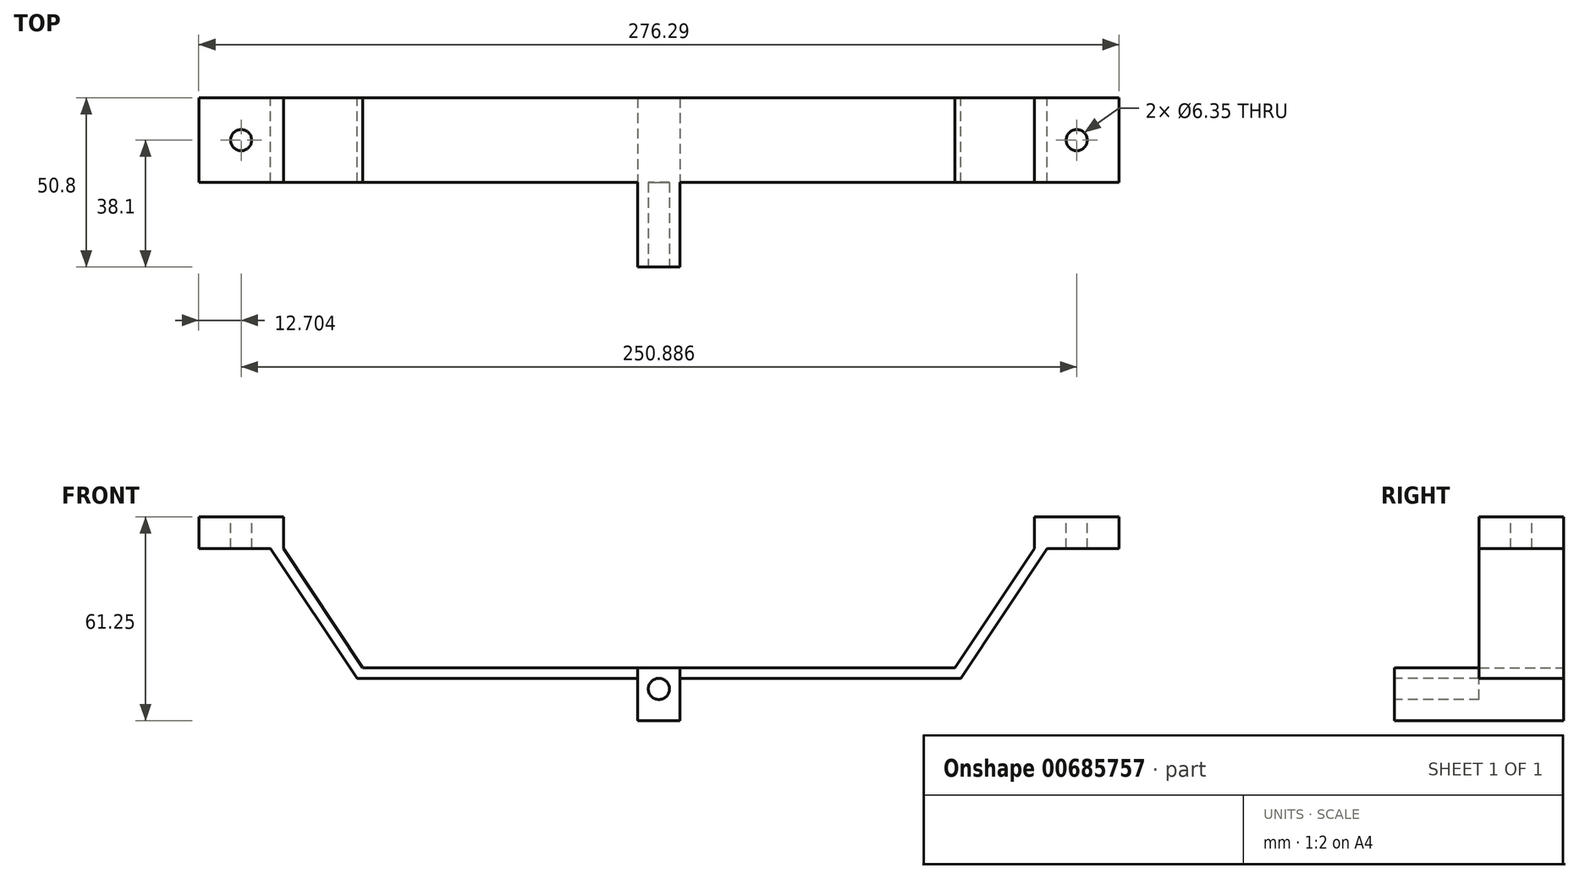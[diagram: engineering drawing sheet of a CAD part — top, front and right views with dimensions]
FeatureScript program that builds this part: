
annotation { "Feature Type Name" : "Feature", "Feature Type Description" : "" }
export const myFeature = defineFeature(function(context is Context, id is Id, definition is map)
    precondition{}
    {
        {
            var Q0;
            Q0=qCreatedBy(makeId("Front.planeOp"),FACE);
            var sketch = newSketch(context, id + "F0", { "sketchPlane" : qUnion([Q0])});
            skLineSegment(sketch, "E0", {"start": v(-83.3, 0) * mm, "end": v(94.5, 0) * mm});
            skLineSegment(sketch, "E1", {"start": v(94.5, 0) * mm, "end": v(118.35, 35.85) * mm});
            skLineSegment(sketch, "E2", {"start": v(-83.3, 0) * mm, "end": v(-107.14, 35.85) * mm});
            skLineSegment(sketch, "E3.bottom", {"start": v(-107.14, 35.85) * mm, "end": v(-132.54, 35.85) * mm});
            skLineSegment(sketch, "E3.top", {"start": v(-107.14, 45.37) * mm, "end": v(-132.54, 45.37) * mm});
            skLineSegment(sketch, "E3.left", {"start": v(-107.14, 35.85) * mm, "end": v(-107.14, 45.37) * mm});
            skLineSegment(sketch, "E3.right", {"start": v(-132.54, 35.85) * mm, "end": v(-132.54, 45.37) * mm});
            skPoint(sketch, "E4.oppositeSnap0", {"position": v(-119.84, 45.37) * mm});
            skLineSegment(sketch, "E4.bottom", {"start": v(118.35, 35.85) * mm, "end": v(143.75, 35.85) * mm});
            skLineSegment(sketch, "E4.top", {"start": v(118.35, 45.37) * mm, "end": v(143.75, 45.37) * mm});
            skLineSegment(sketch, "E4.left", {"start": v(118.35, 35.85) * mm, "end": v(118.35, 45.37) * mm});
            skLineSegment(sketch, "E4.right", {"start": v(143.75, 35.85) * mm, "end": v(143.75, 45.37) * mm});
            skLineSegment(sketch, "E5.0", {"start": v(-85, -3.18) * mm, "end": v(-109.78, 34.1) * mm});
            skLineSegment(sketch, "E5.1", {"start": v(-85, -3.17) * mm, "end": v(96.2, -3.17) * mm});
            skLineSegment(sketch, "E5.2", {"start": v(96.2, -3.18) * mm, "end": v(130.94, 49.04) * mm});
            skLineSegment(sketch, "E6", {"start": v(-109.78, 34.1) * mm, "end": v(-114.55, 41.26) * mm});
            skSolve(sketch);
        }
        {
            var Q0;
            {var subQ0=sQuery(id+"F0.wireOp",EDGE,"xCdVj7Rm-zJCy-WNEK-jx2k-DkXjC7Dfvp6H");Q0=makeQuery(id+"F0.imprint","IMPRINT",FACE,{"disambiguationData":[TD([[makeQuery(id+"F0.imprint","IMPRINT",EDGE,{"derivedFrom":subQ0}),1.0]])]});}
            var Q1;
            {var subQ0=sQuery(id+"F0.wireOp",EDGE,"zULIQO5D-5NXs-XkT0-v7lp-MGDDdhXP3ip7.right");Q1=makeQuery(id+"F0.imprint","IMPRINT",FACE,{"disambiguationData":[TD([[makeQuery(id+"F0.imprint","IMPRINT",EDGE,{"derivedFrom":subQ0}),-1.0]])]});}
            var Q2;
            {var subQ0=sQuery(id+"F0.wireOp",EDGE,"zULIQO5D-5NXs-XkT0-v7lp-MGDDdhXP3ip7.left");Q2=makeQuery(id+"F0.imprint","IMPRINT",FACE,{"disambiguationData":[TD([[makeQuery(id+"F0.imprint","IMPRINT",EDGE,{"derivedFrom":subQ0}),1.0]])]});}
            var Q3;
            {var subQ4=sQuery(id+"F0.wireOp",EDGE,"WJLMLYwR-hRPP-A6Xb-pmzy-IOSkZiBtCFEh.left");Q3=makeQuery(id+"F0.imprint","IMPRINT",FACE,{"disambiguationData":[TD([[makeQuery(id+"F0.imprint","IMPRINT",EDGE,{"derivedFrom":subQ4}),1.0]])]});}
            var Q4;
            {var subQ4=sQuery(id+"F0.wireOp",EDGE,"WJLMLYwR-hRPP-A6Xb-pmzy-IOSkZiBtCFEh.right");Q4=makeQuery(id+"F0.imprint","IMPRINT",FACE,{"disambiguationData":[TD([[makeQuery(id+"F0.imprint","IMPRINT",EDGE,{"derivedFrom":subQ4}),-1.0]])]});}
            var Q5;
            {var subQ0=sQuery(id+"F0.wireOp",EDGE,"45bcc17d-5c14-4652-9b34-e62cf62e381f0.MirrorCS");Q5=makeQuery(id+"F0.imprint","IMPRINT",FACE,{"disambiguationData":[TD([[makeQuery(id+"F0.imprint","IMPRINT",EDGE,{"derivedFrom":subQ0}),1.0]])]});}
            var Q6;
            {var subQ0=sQuery(id+"F0.wireOp",EDGE,"87b93818-efcd-4817-b442-400501f782e70.MirrorCS");Q6=makeQuery(id+"F0.imprint","IMPRINT",FACE,{"disambiguationData":[TD([[makeQuery(id+"F0.imprint","IMPRINT",EDGE,{"derivedFrom":subQ0}),-1.0]])]});}
            var Q7;
            {var subQ1=sQuery(id+"F0.wireOp",EDGE,"772e4d75-e6f5-403f-9652-c3a24cc509a90.MirrorCS");Q7=makeQuery(id+"F0.imprint","IMPRINT",FACE,{"disambiguationData":[TD([[makeQuery(id+"F0.imprint","IMPRINT",EDGE,{"derivedFrom":subQ1}),1.0]])]});}
            var Q8;
            {var subQ4=sQuery(id+"F0.wireOp",EDGE,"8517a0ab-6009-46a5-8872-56797a2ff2e90.MirrorCS");Q8=makeQuery(id+"F0.imprint","IMPRINT",FACE,{"disambiguationData":[TD([[makeQuery(id+"F0.imprint","IMPRINT",EDGE,{"derivedFrom":subQ4}),1.0]])]});}
            var Q9;
            {var subQ1=sQuery(id+"F0.wireOp",EDGE,"7d77567f-4d39-41c3-929c-f897b328c47e0.MirrorCS");Q9=makeQuery(id+"F0.imprint","IMPRINT",FACE,{"disambiguationData":[TD([[makeQuery(id+"F0.imprint","IMPRINT",EDGE,{"derivedFrom":subQ1}),-1.0]])]});}
            var Q10;
            Q10=makeQuery(id+"F0.imprint","IMPRINT",FACE,{"disambiguationData":[TD([[makeQuery(id+"F0.imprint","IMPRINT",EDGE,{"derivedFrom":sQuery(id+"F0.wireOp",EDGE,"E3.top")}),1.0]])]});
            var Q11;
            Q11=makeQuery(id+"F0.imprint","IMPRINT",FACE,{"disambiguationData":[TD([[makeQuery(id+"F0.imprint","IMPRINT",EDGE,{"derivedFrom":sQuery(id+"F0.wireOp",EDGE,"E0")}),-1.0]])]});
            var Q12;
            {var subQ0=sQuery(id+"F0.wireOp",EDGE,"E4.left");Q12=makeQuery(id+"F0.imprint","IMPRINT",FACE,{"disambiguationData":[TD([[makeQuery(id+"F0.imprint","IMPRINT",EDGE,{"derivedFrom":subQ0}),-1.0]])]});}
            var Q13;
            {var subQ0=sQuery(id+"F0.wireOp",EDGE,"E4.right");Q13=makeQuery(id+"F0.imprint","IMPRINT",FACE,{"disambiguationData":[TD([[makeQuery(id+"F0.imprint","IMPRINT",EDGE,{"derivedFrom":subQ0}),1.0]])]});}
            extrude(context, id + "F1", {"entities" : qUnion([Q0, Q1, Q2, Q3, Q4, Q5, Q6, Q7, Q8, Q9, Q10, Q11, Q12, Q13]), "endBound" : BoundingType.SYMMETRIC, "depth" : 25.4 * mm});
        }
        {
            var Q0;
            Q0=makeQuery(id+"F1.opExtrude","CAP_FACE",FACE,{"disambiguationData":[OSD([sQuery(id+"F0.wireOp",EDGE,"E0"),sQuery(id+"F0.wireOp",EDGE,"E1"),sQuery(id+"F0.wireOp",EDGE,"E2"),sQuery(id+"F0.wireOp",EDGE,"E3.bottom"),sQuery(id+"F0.wireOp",EDGE,"E3.top"),sQuery(id+"F0.wireOp",EDGE,"E3.left"),sQuery(id+"F0.wireOp",EDGE,"E3.right"),sQuery(id+"F0.wireOp",EDGE,"E4.bottom"),sQuery(id+"F0.wireOp",EDGE,"E4.top"),sQuery(id+"F0.wireOp",EDGE,"E4.left"),sQuery(id+"F0.wireOp",EDGE,"E4.right"),sQuery(id+"F0.wireOp",EDGE,"E5.0"),sQuery(id+"F0.wireOp",EDGE,"E5.1"),sQuery(id+"F0.wireOp",EDGE,"E5.2"),sQuery(id+"F0.wireOp",EDGE,"E6")])],"isStart":false});
            var sketch = newSketch(context, id + "F2", { "sketchPlane" : qUnion([Q0])});
            skLineSegment(sketch, "E7", {"start": v(5.6, 0) * mm, "end": v(5.6, -15.88) * mm});
            skLineSegment(sketch, "E8", {"start": v(5.6, -15.88) * mm, "end": v(11.96, -15.88) * mm});
            skLineSegment(sketch, "E9", {"start": v(5.6, -15.88) * mm, "end": v(-0.74, -15.88) * mm});
            skLineSegment(sketch, "E10", {"start": v(-0.74, -15.88) * mm, "end": v(-0.74, -3.17) * mm});
            skLineSegment(sketch, "E11", {"start": v(11.96, -15.88) * mm, "end": v(11.96, -3.17) * mm});
            skLineSegment(sketch, "E12", {"start": v(-0.74, -3.17) * mm, "end": v(-0.74, 0) * mm});
            skLineSegment(sketch, "E13", {"start": v(11.96, -3.17) * mm, "end": v(11.96, 0) * mm});
            skLineSegment(sketch, "E14", {"start": v(11.96, 0) * mm, "end": v(0, 0) * mm});
            skLineSegment(sketch, "E15", {"start": v(0, 0) * mm, "end": v(-0.74, 0) * mm});
            skSolve(sketch);
        }
        {
            var Q0;
            {var subQ0=sQuery(id+"F2.wireOp",EDGE,"E9");Q0=makeQuery(id+"F2.imprint","IMPRINT",FACE,{"disambiguationData":[TD([[makeQuery(id+"F2.imprint","IMPRINT",EDGE,{"derivedFrom":subQ0}),-1.0]])]});}
            var Q1;
            {var subQ0=sQuery(id+"F2.wireOp",EDGE,"E8");Q1=makeQuery(id+"F2.imprint","IMPRINT",FACE,{"disambiguationData":[TD([[makeQuery(id+"F2.imprint","IMPRINT",EDGE,{"derivedFrom":subQ0}),1.0]])]});}
            var Q2;
            {var subQ5=sQuery(id+"F2.wireOp",EDGE,"E13");Q2=makeQuery(id+"F2.imprint","IMPRINT",FACE,{"disambiguationData":[TD([[makeQuery(id+"F2.imprint","IMPRINT",EDGE,{"derivedFrom":subQ5}),1.0]])]});}
            var Q3;
            {var subQ4=sQuery(id+"F2.wireOp",EDGE,"E12");Q3=makeQuery(id+"F2.imprint","IMPRINT",FACE,{"disambiguationData":[TD([[makeQuery(id+"F2.imprint","IMPRINT",EDGE,{"derivedFrom":subQ4}),-1.0]])]});}
            extrude(context, id + "F3", {"entities" : qUnion([Q0, Q1, Q2, Q3]), "operationType" : NewBodyOperationType.ADD, "endBound" : BoundingType.SYMMETRIC, "depth" : 50.8 * mm});
        }
        {
            var Q0;
            Q0=makeQuery(id+"F3.opExtrude","CAP_FACE",FACE,{"disambiguationData":[OSD([sQuery(id+"F2.wireOp",EDGE,"E8"),sQuery(id+"F2.wireOp",EDGE,"E9"),sQuery(id+"F2.wireOp",EDGE,"E10"),sQuery(id+"F2.wireOp",EDGE,"E11"),sQuery(id+"F2.wireOp",EDGE,"E12"),sQuery(id+"F2.wireOp",EDGE,"E13"),sQuery(id+"F2.wireOp",EDGE,"E14"),sQuery(id+"F2.wireOp",EDGE,"E15")])],"isStart":false});
            var sketch = newSketch(context, id + "F4", { "sketchPlane" : qUnion([Q0])});
            skPoint(sketch, "E16", {"position": v(5.6, -6.35) * mm});
            skCircle(sketch, "E17", {"center": v(5.6, -6.35) * mm, "radius": 3.18 * mm});
            skSolve(sketch);
        }
        {
            var Q0;
            Q0=makeQuery(id+"F4.imprint","IMPRINT",FACE,{"disambiguationData":[TD([[makeQuery(id+"F4.imprint","IMPRINT",EDGE,{"derivedFrom":sQuery(id+"F4.wireOp",EDGE,"E17")}),1.0]])]});
            extrude(context, id + "F5", {"entities" : qUnion([Q0]), "oppositeDirection" : true, "depth" : 25.4 * mm});
        }
        {
            var Q0;
            Q0=makeQuery(id+"F1.opExtrude","SWEPT_FACE",FACE,{"disambiguationData":[OSD([sQuery(id+"F0.wireOp",EDGE,"E4.top")])]});
            var sketch = newSketch(context, id + "F6", { "sketchPlane" : qUnion([Q0])});
            skPoint(sketch, "E18", {"position": v(131.05, 0) * mm});
            skCircle(sketch, "E19", {"center": v(131.05, 0) * mm, "radius": 3.18 * mm});
            skSolve(sketch);
        }
        {
            var Q0;
            Q0=makeQuery(id+"F6.imprint","IMPRINT",FACE,{"disambiguationData":[TD([[makeQuery(id+"F6.imprint","IMPRINT",EDGE,{"derivedFrom":sQuery(id+"F6.wireOp",EDGE,"E19")}),1.0]])]});
            extrude(context, id + "F7", {"entities" : qUnion([Q0]), "operationType" : NewBodyOperationType.REMOVE, "oppositeDirection" : true, "depth" : 25.4 * mm});
        }
        {
            var Q0;
            Q0=makeQuery(id+"F1.opExtrude","SWEPT_FACE",FACE,{"disambiguationData":[OSD([sQuery(id+"F0.wireOp",EDGE,"E3.top")])]});
            var sketch = newSketch(context, id + "F8", { "sketchPlane" : qUnion([Q0])});
            skPoint(sketch, "E20", {"position": v(-119.84, 0) * mm});
            skCircle(sketch, "E21", {"center": v(-119.84, 0) * mm, "radius": 3.18 * mm});
            skSolve(sketch);
        }
        {
            var Q0;
            Q0=makeQuery(id+"F8.imprint","IMPRINT",FACE,{"disambiguationData":[TD([[makeQuery(id+"F8.imprint","IMPRINT",EDGE,{"derivedFrom":sQuery(id+"F8.wireOp",EDGE,"E21")}),1.0]])]});
            extrude(context, id + "F9", {"entities" : qUnion([Q0]), "operationType" : NewBodyOperationType.REMOVE, "oppositeDirection" : true, "depth" : 25.4 * mm});
        }
    });
